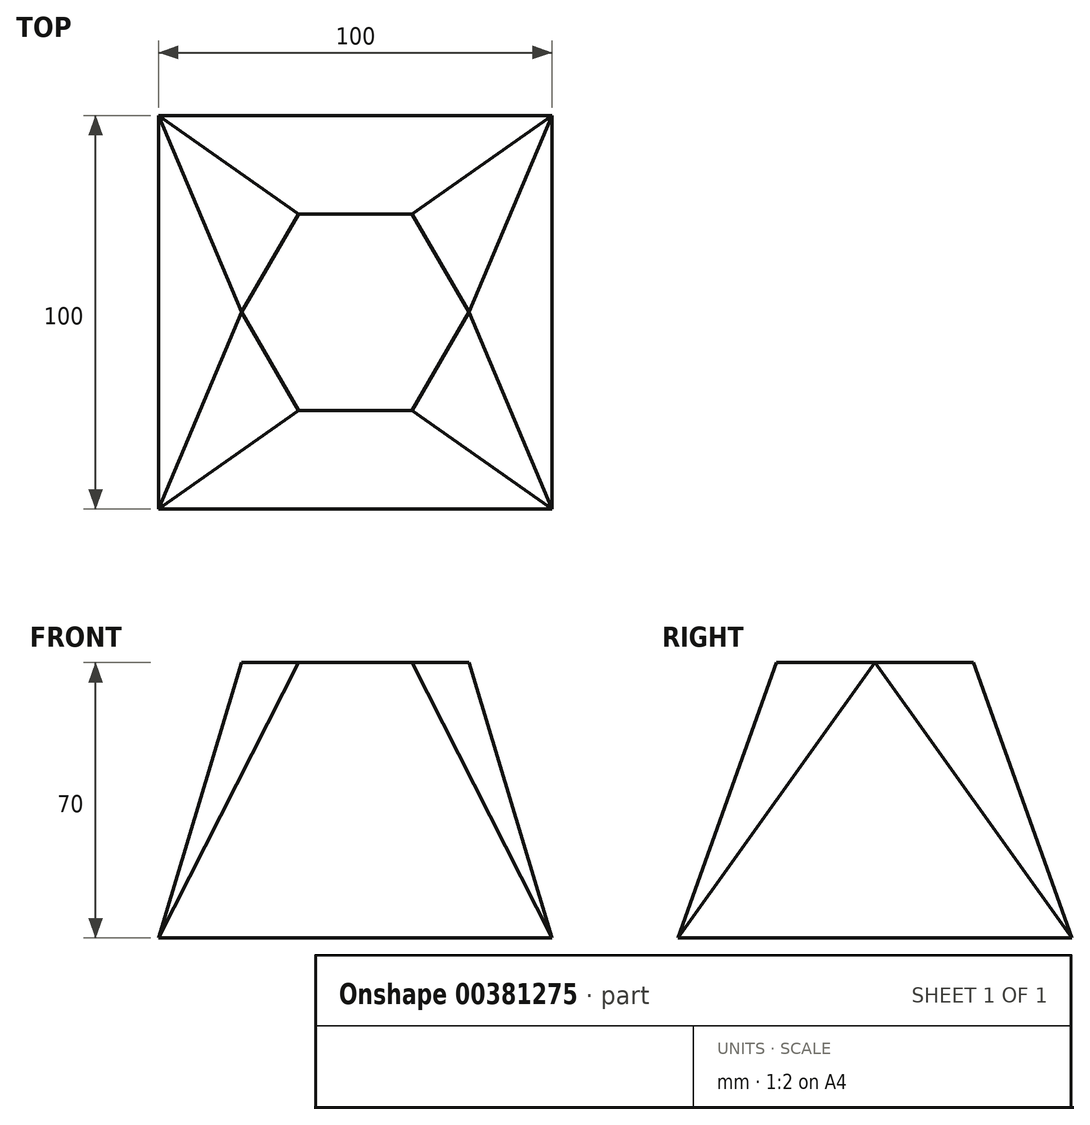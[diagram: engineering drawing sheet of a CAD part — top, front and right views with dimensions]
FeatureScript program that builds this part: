
annotation { "Feature Type Name" : "Feature", "Feature Type Description" : "" }
export const myFeature = defineFeature(function(context is Context, id is Id, definition is map)
    precondition{}
    {
        {
            var Q0;
            Q0=qCreatedBy(makeId("Top.planeOp"),FACE);
            var sketch = newSketch(context, id + "F0", { "sketchPlane" : qUnion([Q0])});
            skLineSegment(sketch, "E0.bottom", {"start": v(-50, 50) * mm, "end": v(50, 50) * mm});
            skLineSegment(sketch, "E0.top", {"start": v(-50, -50) * mm, "end": v(50, -50) * mm});
            skLineSegment(sketch, "E0.left", {"start": v(-50, 50) * mm, "end": v(-50, -50) * mm});
            skLineSegment(sketch, "E0.right", {"start": v(50, 50) * mm, "end": v(50, -50) * mm});
            skPoint(sketch, "E0.middle", {"position": v(0, 0) * mm});
            skSolve(sketch);
        }
        {
            var Q0;
            Q0=qCreatedBy(makeId("Top.planeOp"),FACE);
            cPlane(context, id + "F1", {"entities" : qUnion([Q0]), "cplaneType" : CPlaneType.OFFSET, "offset" : 70 * mm, "width" : 150 * mm, "height" : 150 * mm});
        }
        {
            var Q0;
            Q0=qCreatedBy(id+"F1.planeOp",FACE);
            var sketch = newSketch(context, id + "F2", { "sketchPlane" : qUnion([Q0])});
            skCircle(sketch, "E1.cCircle", {"center": v(0, 0) * mm, "radius": 28.87 * mm, "construction": true});
            skLineSegment(sketch, "E1.0", {"start": v(28.87, 0) * mm, "end": v(14.43, -25) * mm});
            skLineSegment(sketch, "E1.1", {"start": v(14.43, -25) * mm, "end": v(-14.43, -25) * mm});
            skLineSegment(sketch, "E1.2", {"start": v(-14.43, -25) * mm, "end": v(-28.87, 0) * mm});
            skLineSegment(sketch, "E1.3", {"start": v(-28.87, 0) * mm, "end": v(-14.43, 25) * mm});
            skLineSegment(sketch, "E1.4", {"start": v(-14.43, 25) * mm, "end": v(14.43, 25) * mm});
            skLineSegment(sketch, "E1.5", {"start": v(14.43, 25) * mm, "end": v(28.87, 0) * mm});
            skSolve(sketch);
        }
        {
            var Q0;
            Q0=qCreatedBy(id+"F1.planeOp",FACE);
            var sketch = newSketch(context, id + "F3", { "sketchPlane" : qUnion([Q0])});
            skLineSegment(sketch, "E2.bottom", {"start": v(-28.87, 25) * mm, "end": v(28.87, 25) * mm});
            skLineSegment(sketch, "E2.top", {"start": v(-28.87, -25) * mm, "end": v(28.87, -25) * mm});
            skLineSegment(sketch, "E2.left", {"start": v(-28.87, 25) * mm, "end": v(-28.87, -25) * mm});
            skLineSegment(sketch, "E2.right", {"start": v(28.87, 25) * mm, "end": v(28.87, -25) * mm});
            skPoint(sketch, "E2.middle", {"position": v(0, 0) * mm});
            skSolve(sketch);
        }
        {
            var Q0;
            Q0=makeQuery(id+"F0.imprint","IMPRINT",FACE,{"disambiguationData":[TD([[makeQuery(id+"F0.imprint","IMPRINT",EDGE,{"derivedFrom":sQuery(id+"F0.wireOp",EDGE,"E0.bottom")}),-1.0]])]});
            var Q1;
            Q1=makeQuery(id+"F3.imprint","IMPRINT",FACE,{"disambiguationData":[TD([[makeQuery(id+"F3.imprint","IMPRINT",EDGE,{"derivedFrom":sQuery(id+"F3.wireOp",EDGE,"E2.bottom")}),-1.0]])]});
            loft(context, id + "F4", {"sheetProfilesArray" : [{ "sheetProfileEntities" : qUnion([Q0]) }, { "sheetProfileEntities" : qUnion([Q1]) }]});
        }
        {
            var Q0;
            Q0=makeQuery(id+"F3.imprint","IMPRINT",FACE,{"disambiguationData":[TD([[makeQuery(id+"F3.imprint","IMPRINT",EDGE,{"derivedFrom":sQuery(id+"F3.wireOp",EDGE,"E2.bottom")}),-1.0]])]});
            var sketch = newSketch(context, id + "F5", { "sketchPlane" : qUnion([Q0])});
            skLineSegment(sketch, "E3", {"start": v(14.43, 25) * mm, "end": v(28.87, 0) * mm});
            skSolve(sketch);
        }
        {
            var Q1;
            {var subQ0=sQuery(id+"F5.wireOp",EDGE,"E3");Q1=makeQuery(id+"F5.imprint","IMPRINT",FACE,{"disambiguationData":[TD([[makeQuery(id+"F5.imprint","IMPRINT",EDGE,{"derivedFrom":subQ0}),1.0]])]});}
            var Q2;
            Q2=sQuery(id+"F0.wireOp",VERTEX,"E0.bottom.end");
            loft(context, id + "F6", {"sheetProfilesArray" : [{ "sheetProfileEntities" : qUnion([Q1]) }, { "sheetProfileEntities" : qUnion([Q2]) }]});
        }
        {
            var Q0;
            {var subQ0=sQuery(id+"F5.wireOp",EDGE,"E3");Q0=makeQuery(id+"F6.opLoft","SWEPT_BODY",BODY,{"disambiguationData":[OSD([sQuery(id+"F0.wireOp",VERTEX,"E0.bottom.end"),makeQuery(id+"F5.imprint","IMPRINT",FACE,{"disambiguationData":[TD([[makeQuery(id+"F5.imprint","IMPRINT",EDGE,{"derivedFrom":subQ0}),1.0]])]})])]});}
            var Q1;
            Q1=qCreatedBy(makeId("Front.planeOp"),FACE);
            mirror(context, id + "F7", {"entities" : qUnion([Q0]), "mirrorPlane" : qUnion([Q1])});
        }
        {
            var Q0;
            {var subQ0=sQuery(id+"F5.wireOp",EDGE,"E3");Q0=makeQuery(id+"F6.opLoft","SWEPT_BODY",BODY,{"disambiguationData":[OSD([sQuery(id+"F0.wireOp",VERTEX,"E0.bottom.end"),makeQuery(id+"F5.imprint","IMPRINT",FACE,{"disambiguationData":[TD([[makeQuery(id+"F5.imprint","IMPRINT",EDGE,{"derivedFrom":subQ0}),1.0]])]})])]});}
            var Q1;
            {var subQ0=sQuery(id+"F5.wireOp",EDGE,"E3");Q1=makeQuery(id+"F7.opPattern","COPY",BODY,{"derivedFrom":makeQuery(id+"F6.opLoft","SWEPT_BODY",BODY,{"disambiguationData":[OSD([sQuery(id+"F0.wireOp",VERTEX,"E0.bottom.end"),makeQuery(id+"F5.imprint","IMPRINT",FACE,{"disambiguationData":[TD([[makeQuery(id+"F5.imprint","IMPRINT",EDGE,{"derivedFrom":subQ0}),1.0]])]})])]}),"instanceName":"1"});}
            var Q2;
            Q2=qCreatedBy(makeId("Right.planeOp"),FACE);
            mirror(context, id + "F8", {"entities" : qUnion([Q0, Q1]), "mirrorPlane" : qUnion([Q2])});
        }
        {
            var Q0;
            {var subQ0=sQuery(id+"F5.wireOp",EDGE,"E3");Q0=makeQuery(id+"F6.opLoft","SWEPT_BODY",BODY,{"disambiguationData":[OSD([sQuery(id+"F0.wireOp",VERTEX,"E0.bottom.end"),makeQuery(id+"F5.imprint","IMPRINT",FACE,{"disambiguationData":[TD([[makeQuery(id+"F5.imprint","IMPRINT",EDGE,{"derivedFrom":subQ0}),1.0]])]})])]});}
            var Q1;
            {var subQ0=sQuery(id+"F5.wireOp",EDGE,"E3");Q1=makeQuery(id+"F7.opPattern","COPY",BODY,{"derivedFrom":makeQuery(id+"F6.opLoft","SWEPT_BODY",BODY,{"disambiguationData":[OSD([sQuery(id+"F0.wireOp",VERTEX,"E0.bottom.end"),makeQuery(id+"F5.imprint","IMPRINT",FACE,{"disambiguationData":[TD([[makeQuery(id+"F5.imprint","IMPRINT",EDGE,{"derivedFrom":subQ0}),1.0]])]})])]}),"instanceName":"1"});}
            var Q2;
            {var subQ0=sQuery(id+"F5.wireOp",EDGE,"E3");Q2=makeQuery(id+"F8.opPattern","COPY",BODY,{"derivedFrom":makeQuery(id+"F6.opLoft","SWEPT_BODY",BODY,{"disambiguationData":[OSD([sQuery(id+"F0.wireOp",VERTEX,"E0.bottom.end"),makeQuery(id+"F5.imprint","IMPRINT",FACE,{"disambiguationData":[TD([[makeQuery(id+"F5.imprint","IMPRINT",EDGE,{"derivedFrom":subQ0}),1.0]])]})])]}),"instanceName":"1"});}
            var Q3;
            {var subQ0=sQuery(id+"F5.wireOp",EDGE,"E3");Q3=makeQuery(id+"F8.opPattern","COPY",BODY,{"derivedFrom":makeQuery(id+"F7.opPattern","COPY",BODY,{"derivedFrom":makeQuery(id+"F6.opLoft","SWEPT_BODY",BODY,{"disambiguationData":[OSD([sQuery(id+"F0.wireOp",VERTEX,"E0.bottom.end"),makeQuery(id+"F5.imprint","IMPRINT",FACE,{"disambiguationData":[TD([[makeQuery(id+"F5.imprint","IMPRINT",EDGE,{"derivedFrom":subQ0}),1.0]])]})])]}),"instanceName":"1"}),"instanceName":"1"});}
            var Q4;
            Q4=makeQuery(id+"F4.opLoft","SWEPT_BODY",BODY,{"disambiguationData":[OSD([makeQuery(id+"F0.imprint","IMPRINT",FACE,{"disambiguationData":[TD([[makeQuery(id+"F0.imprint","IMPRINT",EDGE,{"derivedFrom":sQuery(id+"F0.wireOp",EDGE,"E0.bottom")}),-1.0]])]}),makeQuery(id+"F3.imprint","IMPRINT",FACE,{"disambiguationData":[TD([[makeQuery(id+"F3.imprint","IMPRINT",EDGE,{"derivedFrom":sQuery(id+"F3.wireOp",EDGE,"E2.bottom")}),-1.0]])]})])]});
            booleanBodies(context, id + "F9", {"operationType" : BooleanOperationType.SUBTRACTION, "tools" : qUnion([Q0, Q1, Q2, Q3]), "targets" : qUnion([Q4])});
        }
    });
